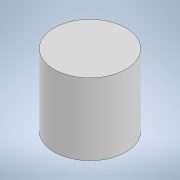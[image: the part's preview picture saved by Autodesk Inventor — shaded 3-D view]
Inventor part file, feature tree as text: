
AUTODESK INVENTOR PART (.ipt)
format: ipt  version: 2020.3 (Build 243373000, 373)  size: 86,528 bytes
history: native  units: mm
features: extrude x1, sketch x1
ambient origin geometry x8: Origin, YZ Plane, XZ Plane, XY Plane, X Axis, Y Axis, Z Axis, Center Point
bodies: Solid1 (feature_tree)
feature tree (2):
  extrude  "Extrusion1"  Depth=32.0mm TaperAngle=0.0deg
  sketch  "Sketch1"  dims[d0=32.0mm d1=32.0mm d2=0.0mm]
